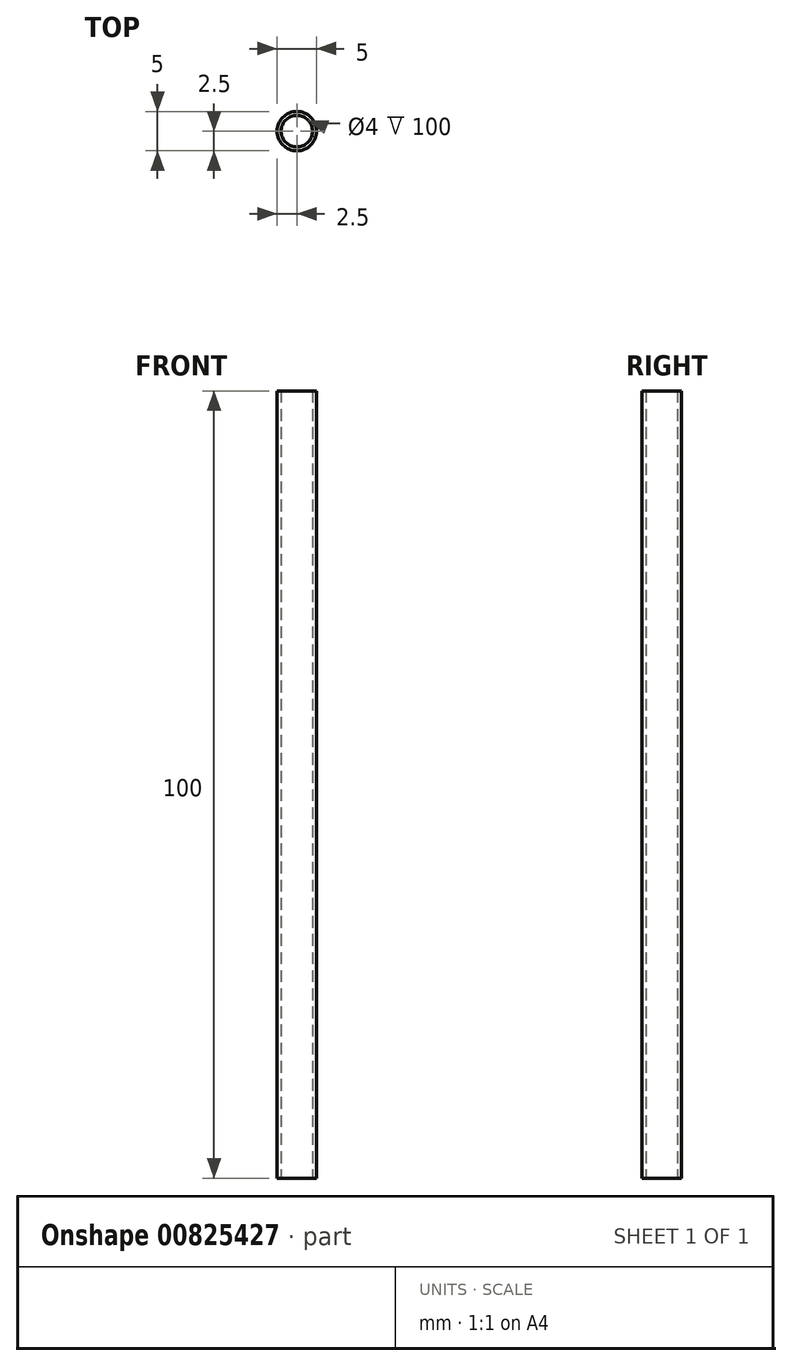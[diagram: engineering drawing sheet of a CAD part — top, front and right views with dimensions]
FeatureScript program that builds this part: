
annotation { "Feature Type Name" : "Feature", "Feature Type Description" : "" }
export const myFeature = defineFeature(function(context is Context, id is Id, definition is map)
    precondition{}
    {
        {
            var Q0;
            Q0=qCreatedBy(makeId("Top.planeOp"),FACE);
            var sketch = newSketch(context, id + "F0", { "sketchPlane" : qUnion([Q0])});
            skCircle(sketch, "E0", {"center": v(0, 0) * mm, "radius": 2.5 * mm});
            skSolve(sketch);
        }
        {
            var Q0;
            Q0=makeQuery(id+"F0.imprint","IMPRINT",FACE,{"disambiguationData":[TD([[makeQuery(id+"F0.imprint","IMPRINT",EDGE,{"derivedFrom":sQuery(id+"F0.wireOp",EDGE,"E0")}),1.0]])]});
            var Q1;
            Q1=sQuery(id+"F0.wireOp",EDGE,"E0");
            extrude(context, id + "F1", {"entities" : qUnion([Q0]), "surfaceEntities" : qUnion([Q1]), "depth" : 100 * mm, "offsetDistance" : 25 * mm});
        }
        {
            var Q0;
            Q0=qCreatedBy(makeId("Top.planeOp"),FACE);
            var sketch = newSketch(context, id + "F2", { "sketchPlane" : qUnion([Q0])});
            skCircle(sketch, "E1", {"center": v(0, 0) * mm, "radius": 2 * mm});
            skSolve(sketch);
        }
        {
            var Q0;
            Q0=makeQuery(id+"F2.imprint","IMPRINT",FACE,{"disambiguationData":[TD([[makeQuery(id+"F2.imprint","IMPRINT",EDGE,{"derivedFrom":sQuery(id+"F2.wireOp",EDGE,"E1")}),1.0]])]});
            var Q1;
            Q1=sQuery(id+"F2.wireOp",EDGE,"E1");
            extrude(context, id + "F3", {"entities" : qUnion([Q0]), "operationType" : NewBodyOperationType.REMOVE, "surfaceEntities" : qUnion([Q1]), "endBound" : BoundingType.THROUGH_ALL, "depth" : 25 * mm, "offsetDistance" : 25 * mm});
        }
    });
